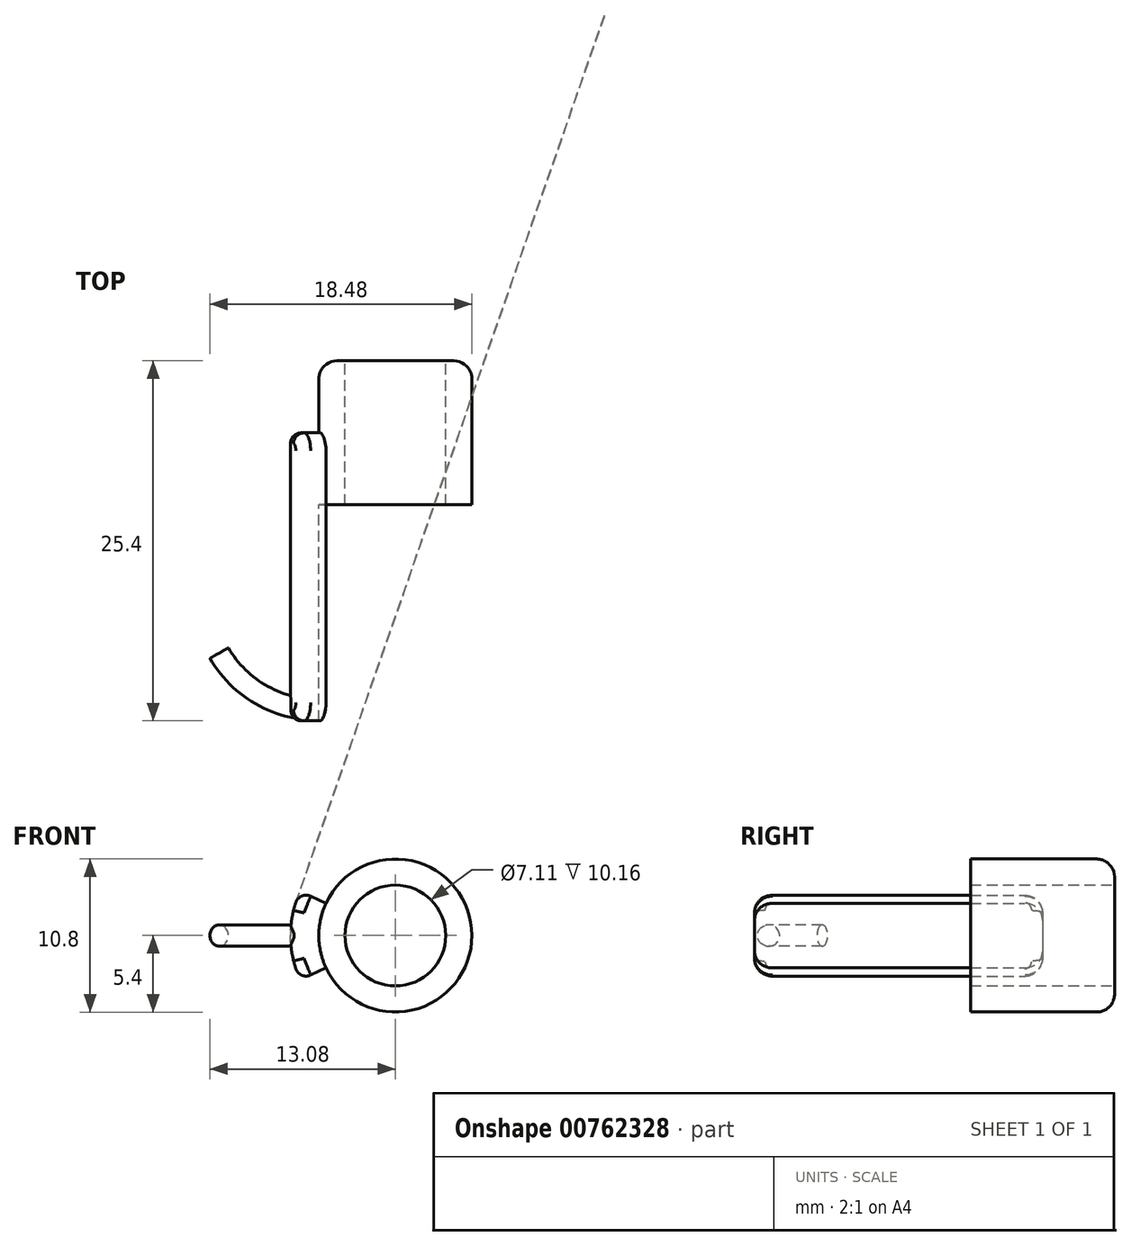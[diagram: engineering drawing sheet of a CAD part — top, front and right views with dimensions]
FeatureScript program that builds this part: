
annotation { "Feature Type Name" : "Feature", "Feature Type Description" : "" }
export const myFeature = defineFeature(function(context is Context, id is Id, definition is map)
    precondition{}
    {
        {
            var Q0;
            Q0=qCreatedBy(makeId("Front.planeOp"),FACE);
            var sketch = newSketch(context, id + "F0", { "sketchPlane" : qUnion([Q0])});
            skCircle(sketch, "E0", {"center": v(0, 0) * mm, "radius": 5.4 * mm});
            skCircle(sketch, "E1", {"center": v(0, 0) * mm, "radius": 3.56 * mm});
            skSolve(sketch);
        }
        {
            var Q0;
            Q0=qSketchRegion(id+"F0",true);
            extrude(context, id + "F1", {"entities" : qUnion([Q0]), "depth" : 10.16 * mm});
        }
        {
            var Q0;
            Q0=qCreatedBy(makeId("Front.planeOp"),FACE);
            cPlane(context, id + "F2", {"entities" : qUnion([Q0]), "cplaneType" : CPlaneType.OFFSET, "offset" : 5.08 * mm, "width" : 152.4 * mm, "height" : 152.4 * mm});
        }
        {
            var Q0;
            Q0=qCreatedBy(id+"F2.planeOp",FACE);
            var sketch = newSketch(context, id + "F3", { "sketchPlane" : qUnion([Q0])});
            skArc(sketch, "E2", {"start": v(-4.9, 2.28) * mm, "mid": v(-5.4, 0) * mm, "end": v(-4.89, -2.29) * mm});
            skArc(sketch, "E3", {"start": v(-6.7, 3.12) * mm, "mid": v(-7.4, 0) * mm, "end": v(-6.7, -3.13) * mm});
            skLineSegment(sketch, "E4", {"start": v(-6.7, 3.12) * mm, "end": v(-4.9, 2.28) * mm});
            skLineSegment(sketch, "E5", {"start": v(-4.89, -2.29) * mm, "end": v(-6.7, -3.13) * mm});
            skSolve(sketch);
        }
        {
            var Q0;
            Q0=qSketchRegion(id+"F3",true);
            extrude(context, id + "F4", {"entities" : qUnion([Q0]), "operationType" : NewBodyOperationType.ADD, "depth" : 20.32 * mm});
        }
        {
            var Q0;
            Q0=qCreatedBy(makeId("Right.planeOp"),FACE);
            cPlane(context, id + "F5", {"entities" : qUnion([Q0]), "cplaneType" : CPlaneType.OFFSET, "offset" : 5.5 * mm, "oppositeDirection" : true, "width" : 152.4 * mm, "height" : 152.4 * mm});
        }
        {
            var Q0;
            Q0=makeQuery(id+"F4.opExtrude","CAP_EDGE",EDGE,{"disambiguationData":[OSD([sQuery(id+"F3.wireOp",EDGE,"E5")])],"isStart":false});
            fillet(context, id + "F6", {"entities" : qUnion([Q0]), "radius" : 1.27 * mm, "tangentPropagation" : true, "allowEdgeOverflow" : false});
        }
        {
            var Q0;
            Q0=makeQuery(id+"F4.opExtrude","CAP_EDGE",EDGE,{"disambiguationData":[OSD([sQuery(id+"F3.wireOp",EDGE,"E4")])],"isStart":false});
            fillet(context, id + "F7", {"entities" : qUnion([Q0]), "radius" : 1.27 * mm, "tangentPropagation" : true, "allowEdgeOverflow" : false});
        }
        {
            var Q0;
            Q0=makeQuery(id+"F4.opExtrude","SWEPT_EDGE",EDGE,{"disambiguationData":[OSD([sQuery(id+"F3.wireOp",EDGE,"E3"),sQuery(id+"F3.wireOp",EDGE,"E5")])]});
            var Q1;
            Q1=makeQuery(id+"F4.opExtrude","CAP_EDGE",EDGE,{"disambiguationData":[OSD([sQuery(id+"F3.wireOp",EDGE,"E3")])],"isStart":true});
            fillet(context, id + "F8", {"entities" : qUnion([Q0, Q1]), "radius" : 0.76 * mm, "tangentPropagation" : true, "allowEdgeOverflow" : false});
        }
        {
            var Q0;
            Q0=makeQuery(id+"F4.opExtrude","CAP_EDGE",EDGE,{"disambiguationData":[OSD([sQuery(id+"F3.wireOp",EDGE,"E4")])],"isStart":true});
            var Q1;
            Q1=makeQuery(id+"F4.opExtrude","CAP_EDGE",EDGE,{"disambiguationData":[OSD([sQuery(id+"F3.wireOp",EDGE,"E5")])],"isStart":true});
            fillet(context, id + "F9", {"entities" : qUnion([Q0, Q1]), "radius" : 1.27 * mm, "tangentPropagation" : true, "allowEdgeOverflow" : false});
        }
        {
            var Q0;
            Q0=makeQuery(id+"F1.opExtrude","CAP_EDGE",EDGE,{"disambiguationData":[OSD([sQuery(id+"F0.wireOp",EDGE,"E0")])],"isStart":true});
            fillet(context, id + "F10", {"entities" : qUnion([Q0]), "radius" : 1.27 * mm, "tangentPropagation" : true, "allowEdgeOverflow" : false});
        }
        {
            var Q0;
            Q0=qCreatedBy(id+"F5.planeOp",FACE);
            var sketch = newSketch(context, id + "F11", { "sketchPlane" : qUnion([Q0])});
            skCircle(sketch, "E6", {"center": v(-24.62, 0) * mm, "radius": 0.75 * mm});
            skLineSegment(sketch, "E7", {"start": v(-16.62, 5.02) * mm, "end": v(-16.62, -5.05) * mm});
            skSolve(sketch);
        }
        {
            var Q0;
            Q0=makeQuery(id+"F11.imprint","IMPRINT",FACE,{"disambiguationData":[TD([[makeQuery(id+"F11.imprint","IMPRINT",EDGE,{"derivedFrom":sQuery(id+"F11.wireOp",EDGE,"E6")}),1.0]])]});
            var Q1;
            Q1=sQuery(id+"F11.wireOp",EDGE,"E7");
            revolve(context, id + "F12", {"operationType" : NewBodyOperationType.ADD, "surfaceOperationType" : NewSurfaceOperationType.NEW, "entities" : qUnion([Q0]), "axis" : qUnion([Q1]), "revolveType" : RevolveType.ONE_DIRECTION, "angle" : 60 * degree});
        }
    });
